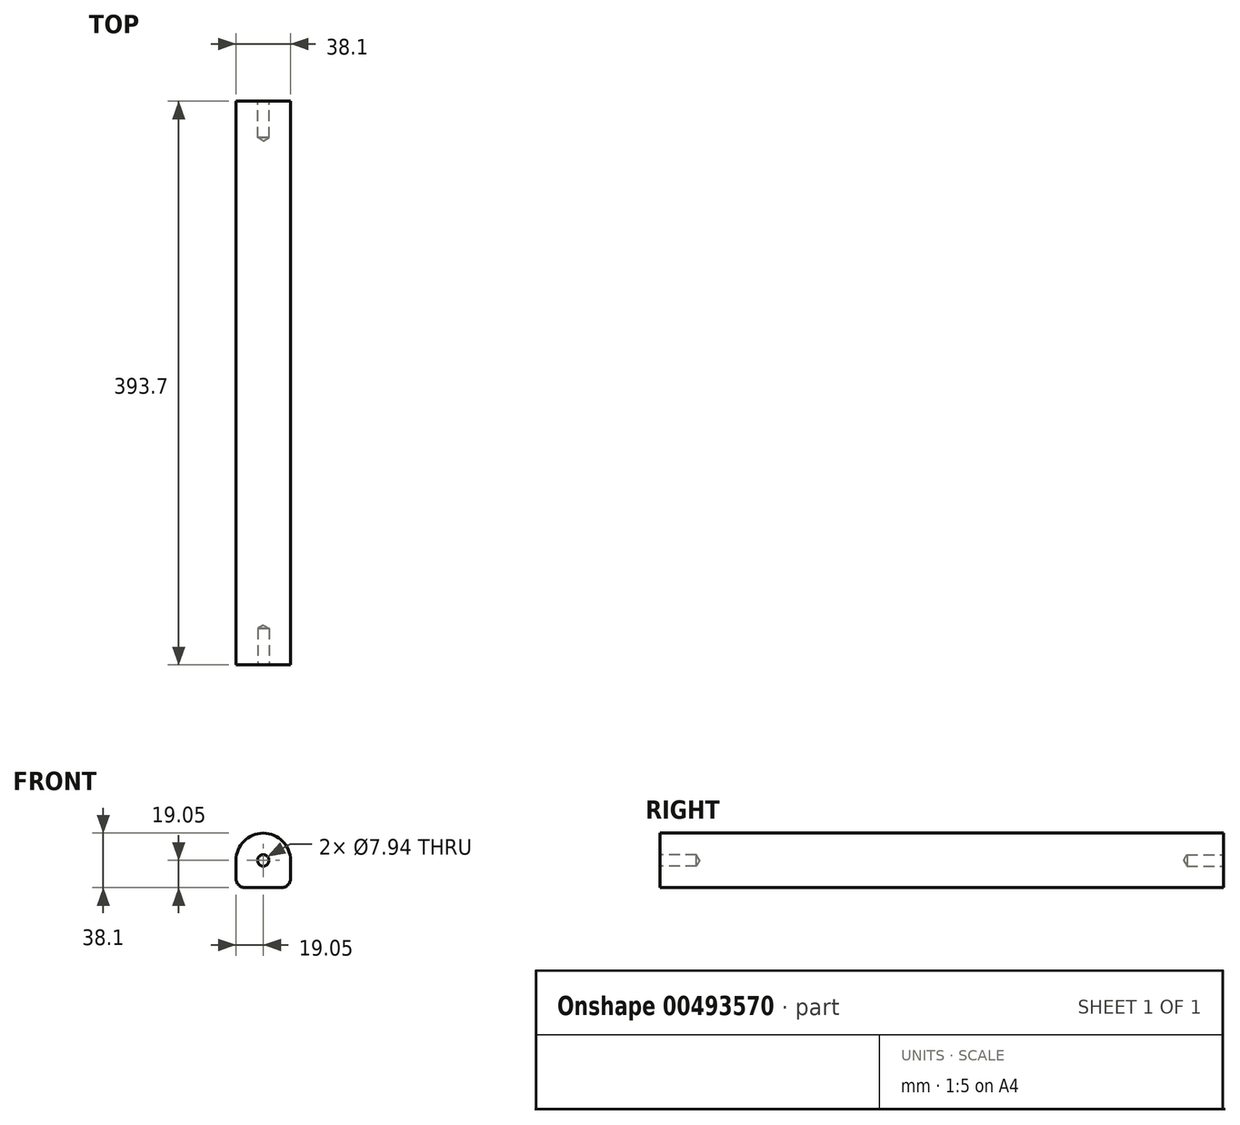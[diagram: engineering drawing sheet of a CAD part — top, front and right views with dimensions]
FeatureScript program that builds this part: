
annotation { "Feature Type Name" : "Feature", "Feature Type Description" : "" }
export const myFeature = defineFeature(function(context is Context, id is Id, definition is map)
    precondition{}
    {
        {
            var Q0;
            Q0=qCreatedBy(makeId("Front.planeOp"),FACE);
            var sketch = newSketch(context, id + "F0", { "sketchPlane" : qUnion([Q0])});
            skLineSegment(sketch, "E0.bottom", {"start": v(6.35, 0) * mm, "end": v(31.75, 0) * mm});
            skLineSegment(sketch, "E0.left", {"start": v(0, 6.35) * mm, "end": v(0, 19.05) * mm});
            skLineSegment(sketch, "E0.right", {"start": v(38.1, 6.35) * mm, "end": v(38.1, 19.05) * mm});
            skArc(sketch, "E1", {"start": v(38.1, 19.05) * mm, "mid": v(19.05, 38.1) * mm, "end": v(0, 19.05) * mm});
            skPoint(sketch, "E2.visualSharp", {"position": v(0, 0) * mm});
            skArc(sketch, "E2.filletArc", {"start": v(0, 6.35) * mm, "mid": v(1.86, 1.86) * mm, "end": v(6.35, 0) * mm});
            skPoint(sketch, "E3.visualSharp", {"position": v(38.1, 0) * mm});
            skArc(sketch, "E3.filletArc", {"start": v(31.75, 0) * mm, "mid": v(36.24, 1.86) * mm, "end": v(38.1, 6.35) * mm});
            skSolve(sketch);
        }
        {
            var Q0;
            Q0 = qSketchRegion(id + "F0", true);
            extrude(context, id + "F1", {"entities" : qUnion([Q0]), "depth" : 393.7 * mm});
        }
        {
            var Q0;
            Q0=makeQuery(id+"F1.opExtrude","CAP_FACE",FACE,{"disambiguationData":[OSD([sQuery(id+"F0.wireOp",EDGE,"E0.bottom"),sQuery(id+"F0.wireOp",EDGE,"E0.left"),sQuery(id+"F0.wireOp",EDGE,"E0.right"),sQuery(id+"F0.wireOp",EDGE,"E1"),sQuery(id+"F0.wireOp",EDGE,"E2.filletArc"),sQuery(id+"F0.wireOp",EDGE,"E3.filletArc")])],"isStart":false});
            var sketch = newSketch(context, id + "F2", { "sketchPlane" : qUnion([Q0])});
            skPoint(sketch, "E4", {"position": v(19.05, 19.05) * mm});
            skSolve(sketch);
        }
        {
            var Q0;
            Q0=makeQuery(id+"F1.opExtrude","CAP_FACE",FACE,{"disambiguationData":[OSD([sQuery(id+"F0.wireOp",EDGE,"E0.bottom"),sQuery(id+"F0.wireOp",EDGE,"E0.left"),sQuery(id+"F0.wireOp",EDGE,"E0.right"),sQuery(id+"F0.wireOp",EDGE,"E1"),sQuery(id+"F0.wireOp",EDGE,"E2.filletArc"),sQuery(id+"F0.wireOp",EDGE,"E3.filletArc")])],"isStart":true});
            var sketch = newSketch(context, id + "F3", { "sketchPlane" : qUnion([Q0])});
            skPoint(sketch, "E5", {"position": v(-19.05, 19.05) * mm});
            skSolve(sketch);
        }
        {
            var Q0;
            Q0=sQuery(id+"F2.wireOp",VERTEX,"E4");
            var Q1;
            Q1=sQuery(id+"F3.wireOp",VERTEX,"E5");
            var Q2;
            Q2=makeQuery(id+"F1.opExtrude","SWEPT_BODY",BODY,{"disambiguationData":[OSD([sQuery(id+"F0.wireOp",EDGE,"E0.bottom"),sQuery(id+"F0.wireOp",EDGE,"E0.left"),sQuery(id+"F0.wireOp",EDGE,"E0.right"),sQuery(id+"F0.wireOp",EDGE,"E1"),sQuery(id+"F0.wireOp",EDGE,"E2.filletArc"),sQuery(id+"F0.wireOp",EDGE,"E3.filletArc")])]});
            hole(context, id + "F4", {"style" : HoleStyle.SIMPLE, "endStyle" : HoleEndStyle.BLIND, "standardTappedOrClearance" : lookupTablePath({ "standard" : "ANSI", "engagement" : "75%", "pitch" : "16 tpi", "size" : "3/8", "type" : "Tapped" }), "standardBlindInLast" : lookupTablePath({ "standard" : "ANSI", "engagement" : "75%", "pitch" : "16 tpi", "size" : "3/8", "type" : "Tapped" }), "holeDiameter" : 7.94 * mm, "showTappedDepth" : true, "holeDepth" : 25.4 * mm, "tappedDepth" : 20.64 * mm, "tapClearance" : 3, "startFromSketch" : true, "locations" : qUnion([Q0, Q1]), "scope" : qUnion([Q2]), "majorDiameter" : 9.53 * mm});
        }
    });
